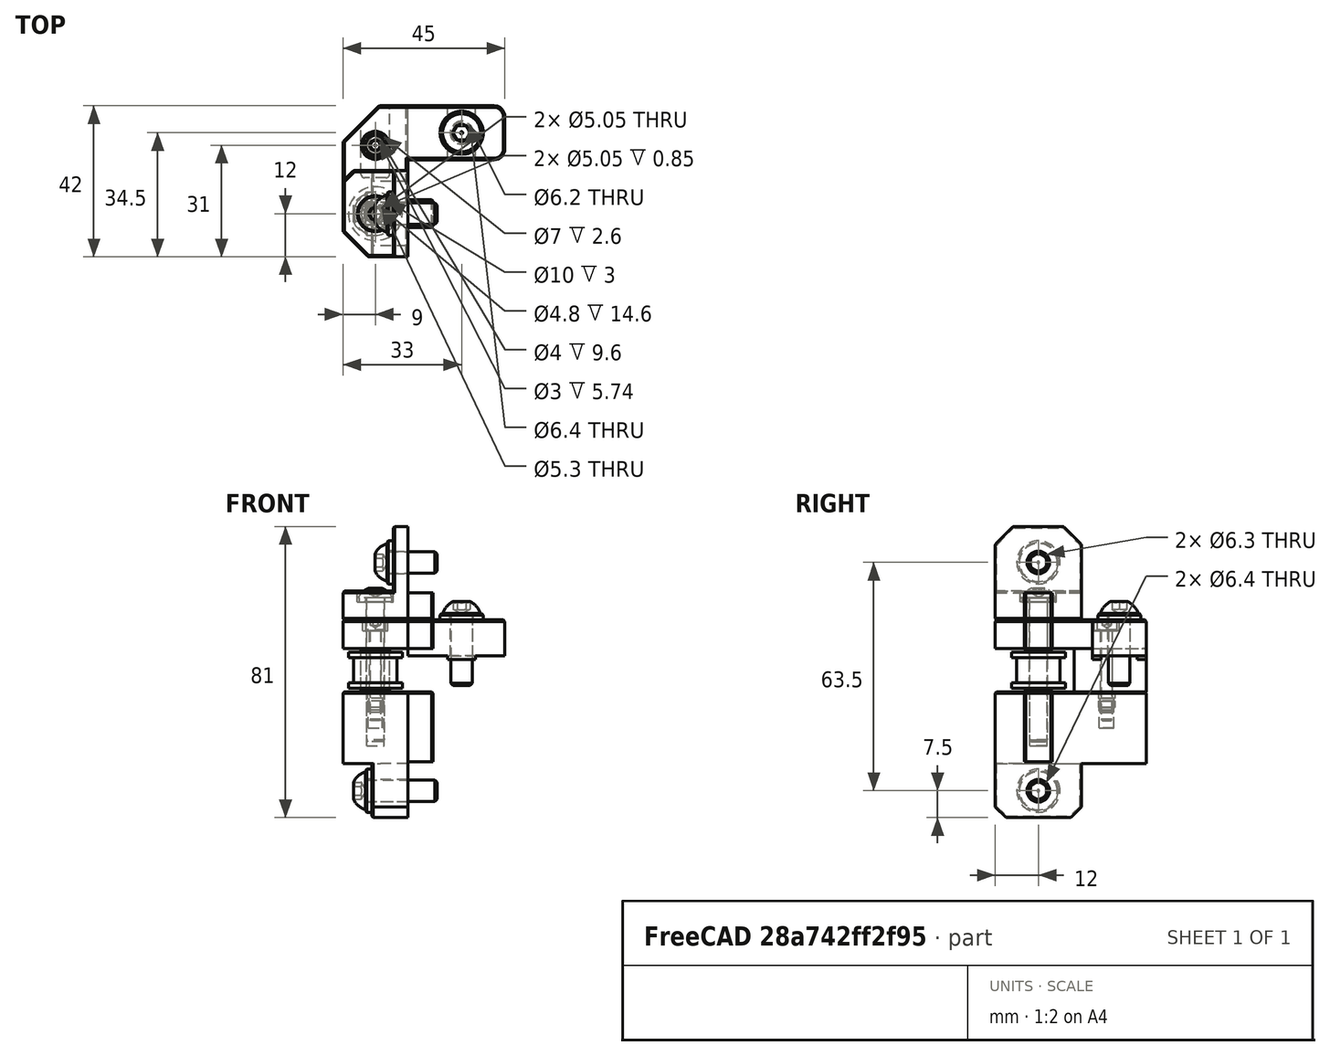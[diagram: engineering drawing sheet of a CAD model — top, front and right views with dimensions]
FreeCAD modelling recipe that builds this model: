
FCSTD DOCUMENT  (FreeCAD 0.19R24291 (Git))
Label: front-right-idler-assembly
License: Other
LicenseURL: GPL3
objects: Part::FeaturePython×10, Part::Feature×6, PartDesign::CoordinateSystem×1, App::Part×1
note: 17 computed .brp shape members not serialized (recipe doc carries the construction recipe); baked Part::Feature solids carry a one-line shape summary decoded from their .brp

FEATURE [Part::Feature] Part__Mirroring004002  label="smooth-idler-6mm"
  Placement = pos=(2,0,0) rot=(0,0,1;0rad)
  shape: bbox 15 x 15 x 10 mm, 8 faces (baked)
FEATURE [Part::Feature] Part__Mirroring003001  label="front-idler-spacer003"
  Placement = pos=(2,0,0) rot=(0,0,1;0rad)
  shape: bbox 8 x 8 x 0.85 mm, 4 faces (baked)
FEATURE [Part::Feature] Part__Mirroring004001  label="front-idler-spacer002"
  Placement = pos=(2,0,0) rot=(0,0,1;0rad)
  shape: bbox 8 x 8 x 0.85 mm, 4 faces (baked)
FEATURE [Part::FeaturePython] Screw  label="M3x25-Screw"  # Fasteners workbench fastener (typed FeaturePython)
  Placement = pos=(-9,34,37) rot=(0,0,1;0rad)
  diameter = 4
  invert = true
  length = 10
  lengthCustom = 25
  matchOuter = true
  offset = 0
  thread = false
  type = 33
FEATURE [Part::FeaturePython] Washer  label="M6-Washer"  # Fasteners workbench fastener (typed FeaturePython)
  Placement = pos=(15,37.5,40) rot=(0,0,1;0rad)
  diameter = 2
  invert = true
  matchOuter = true
  offset = 0
  type = 4
FEATURE [Part::FeaturePython] Screw001  label="M6x20-Screw"  # Fasteners workbench fastener (typed FeaturePython)
  Placement = pos=(15,37.5,41.8) rot=(0,0,1;0rad)
  baseObject = -> Washer [Edge1]
  diameter = 4
  invert = false
  length = 4
  lengthCustom = 20
  matchOuter = true
  offset = 0
  thread = false
  type = 39
FEATURE [Part::FeaturePython] Washer001  label="M6-Washer009"  # Fasteners workbench fastener (typed FeaturePython)
  Placement = pos=(-10,15,-7.5) rot=(0,-1,0;1.5708rad)
  diameter = 2
  invert = true
  matchOuter = true
  offset = 0
  type = 4
FEATURE [Part::FeaturePython] Screw003  label="M6x20-Screw001"  # Fasteners workbench fastener (typed FeaturePython)
  Placement = pos=(-11.8,15,-7.5) rot=(0,-1,0;1.5708rad)
  baseObject = -> Washer001 [Edge1]
  diameter = 4
  invert = false
  length = 4
  lengthCustom = 20
  matchOuter = true
  offset = 0
  thread = false
  type = 39
FEATURE [Part::FeaturePython] Washer005  label="M6-Washer010"  # Fasteners workbench fastener (typed FeaturePython)
  Placement = pos=(-4,15,56) rot=(0,-1,0;1.5708rad)
  diameter = 2
  invert = false
  matchOuter = true
  offset = 0
  type = 4
FEATURE [Part::FeaturePython] Screw009  label="M6x14-Screw"  # Fasteners workbench fastener (typed FeaturePython)
  Placement = pos=(-5.8,15,56) rot=(0,-1,0;1.5708rad)
  baseObject = -> Washer005 [Edge1]
  diameter = 4
  invert = false
  length = 2
  lengthCustom = 14
  matchOuter = true
  offset = 0
  thread = false
  type = 39
FEATURE [Part::FeaturePython] HeatSet001  label="M3x4-HeatSet001"  # WARN: FeaturePython — macro-defined, semantics opaque (R4)
  Placement = pos=(-9,34,20) rot=(0,0,1;0rad)
  diameter = 2
  invert = true
  offset = 0
FEATURE [Part::FeaturePython] Washer006  label="M5-Washer"  # Fasteners workbench fastener (typed FeaturePython)
  Placement = pos=(-9,15,45) rot=(0,0,1;0rad)
  diameter = 6
  invert = true
  matchOuter = true
  offset = 0
  type = 5
FEATURE [PartDesign::CoordinateSystem] LCS_right_idler  label="LCS_right-idler"
  AttacherType = Attacher::AttachEngine3D
FEATURE [Part::FeaturePython] Screw016  label="M5x40-Screw"  # Fasteners workbench fastener (typed FeaturePython)
  Placement = pos=(-9,15,46.1) rot=(0,0,1;0rad)
  baseObject = -> Washer006 [Edge1]
  diameter = 3
  invert = false
  length = 9
  lengthCustom = 40
  matchOuter = false
  offset = 0
  thread = false
  type = 40
FEATURE [Part::Feature] Part__Mirroring002002  label="right-idler-bottom"
  shape: bbox 25 x 42 x 35 mm, 51 faces (baked)
FEATURE [Part::Feature] Part__Mirroring002001  label="right-idler-mid"
  shape: bbox 45 x 42 x 20 mm, 66 faces (baked)
FEATURE [Part::Feature] Part__Mirroring003  label="right-idler-top"
  shape: bbox 25 x 24 x 26 mm, 64 faces (baked)
FEATURE [App::Part] Part001  label="right-idler"
  Group = -> [Part__Mirroring004002,Part__Mirroring003001,Part__Mirroring004001,Washer,Screw001,Screw,Screw003,Washer001,Washer006,Screw009,Washer005,HeatSet001,LCS_right_idler,Screw016,Part__Mirroring002002,Part__Mirroring002001,Part__Mirroring003]
  Origin = -> Origin001
